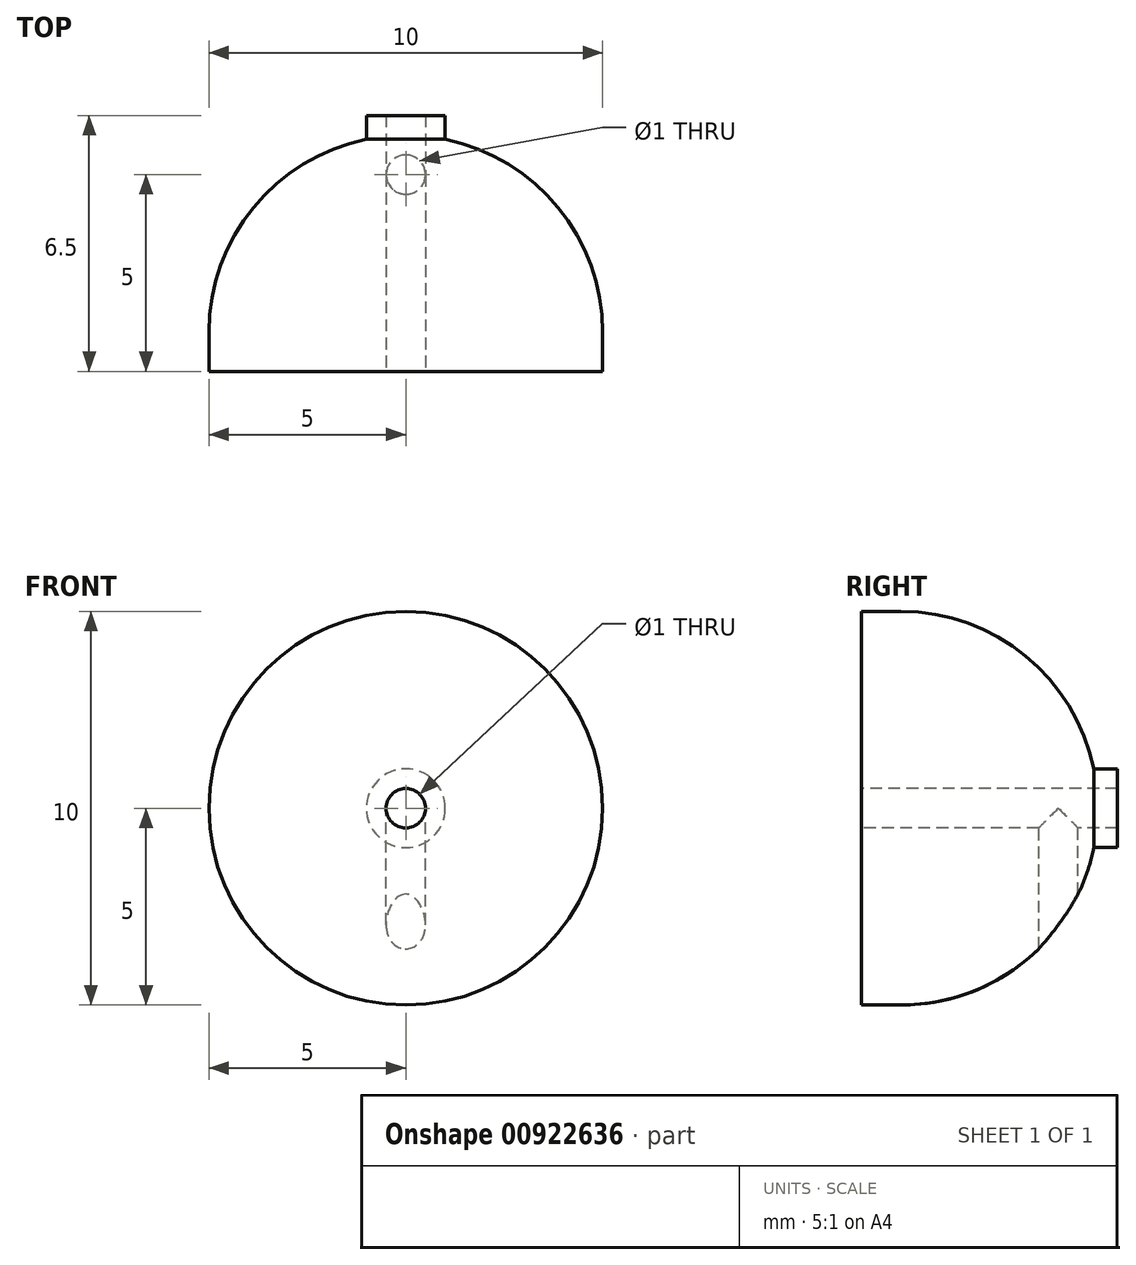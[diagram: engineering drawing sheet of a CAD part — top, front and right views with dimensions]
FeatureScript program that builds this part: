
annotation { "Feature Type Name" : "Feature", "Feature Type Description" : "" }
export const myFeature = defineFeature(function(context is Context, id is Id, definition is map)
    precondition{}
    {
        {
            var Q0;
            Q0=qCreatedBy(makeId("Front.planeOp"),FACE);
            var sketch = newSketch(context, id + "F0", { "sketchPlane" : qUnion([Q0])});
            skCircle(sketch, "E0", {"center": v(0, 0) * mm, "radius": 5 * mm});
            skSolve(sketch);
        }
        {
            var Q0;
            Q0=makeQuery(id+"F0.imprint","IMPRINT",FACE,{"disambiguationData":[TD([[makeQuery(id+"F0.imprint","IMPRINT",EDGE,{"derivedFrom":sQuery(id+"F0.wireOp",EDGE,"E0")}),1.0]])]});
            extrude(context, id + "F1", {"entities" : qUnion([Q0]), "depth" : 6 * mm, "offsetDistance" : 25 * mm});
        }
        {
            var Q0;
            Q0=qCreatedBy(makeId("Top.planeOp"),FACE);
            var sketch = newSketch(context, id + "F2", { "sketchPlane" : qUnion([Q0])});
            skCircle(sketch, "E1", {"center": v(0, -1) * mm, "radius": 0.5 * mm});
            skSolve(sketch);
        }
        {
            var Q0;
            Q0=makeQuery(id+"F2.imprint","IMPRINT",FACE,{"disambiguationData":[TD([[makeQuery(id+"F2.imprint","IMPRINT",EDGE,{"derivedFrom":sQuery(id+"F2.wireOp",EDGE,"E1")}),1.0]])]});
            extrude(context, id + "F3", {"entities" : qUnion([Q0]), "operationType" : NewBodyOperationType.REMOVE, "oppositeDirection" : true, "depth" : 5 * mm, "offsetDistance" : 25 * mm});
        }
        {
            var Q0;
            Q0=makeQuery(id+"F1.opExtrude","CAP_EDGE",EDGE,{"disambiguationData":[OSD([sQuery(id+"F0.wireOp",EDGE,"E0")])],"isStart":true});
            fillet(context, id + "F4", {"entities" : qUnion([Q0]), "radius" : 5 * mm, "tangentPropagation" : true, "allowEdgeOverflow" : false});
        }
        {
            var Q0;
            Q0=makeQuery(id+"F1.opExtrude","CAP_FACE",FACE,{"disambiguationData":[OSD([sQuery(id+"F0.wireOp",EDGE,"E0")])],"isStart":false});
            var sketch = newSketch(context, id + "F5", { "sketchPlane" : qUnion([Q0])});
            skCircle(sketch, "E2", {"center": v(0, 0) * mm, "radius": 0.5 * mm});
            skSolve(sketch);
        }
        {
            var Q0;
            Q0=makeQuery(id+"F5.imprint","IMPRINT",FACE,{"disambiguationData":[TD([[makeQuery(id+"F5.imprint","IMPRINT",EDGE,{"derivedFrom":sQuery(id+"F5.wireOp",EDGE,"E2")}),1.0]])]});
            extrude(context, id + "F6", {"entities" : qUnion([Q0]), "operationType" : NewBodyOperationType.REMOVE, "oppositeDirection" : true, "depth" : 6 * mm, "offsetDistance" : 25 * mm});
        }
        {
            var Q0;
            Q0=qCreatedBy(makeId("Front.planeOp"),FACE);
            var sketch = newSketch(context, id + "F7", { "sketchPlane" : qUnion([Q0])});
            skCircle(sketch, "E3", {"center": v(0, 0) * mm, "radius": 0.5 * mm});
            skCircle(sketch, "E4", {"center": v(0, 0) * mm, "radius": 1 * mm});
            skSolve(sketch);
        }
        {
            var Q0;
            Q0=qCreatedBy(makeId("Front.planeOp"),FACE);
            cPlane(context, id + "F8", {"entities" : qUnion([Q0]), "cplaneType" : CPlaneType.OFFSET, "offset" : 1 * mm, "oppositeDirection" : true, "width" : 150 * mm, "height" : 150 * mm});
        }
        {
            var Q0;
            Q0=makeQuery(id+"F7.imprint","IMPRINT",FACE,{"disambiguationData":[TD([[makeQuery(id+"F7.imprint","IMPRINT",EDGE,{"derivedFrom":sQuery(id+"F7.wireOp",EDGE,"E3")}),-1.0]])]});
            extrude(context, id + "F9", {"entities" : qUnion([Q0]), "operationType" : NewBodyOperationType.ADD, "endBound" : BoundingType.SYMMETRIC, "oppositeDirection" : true, "depth" : 1 * mm, "offsetDistance" : 25 * mm});
        }
    });
